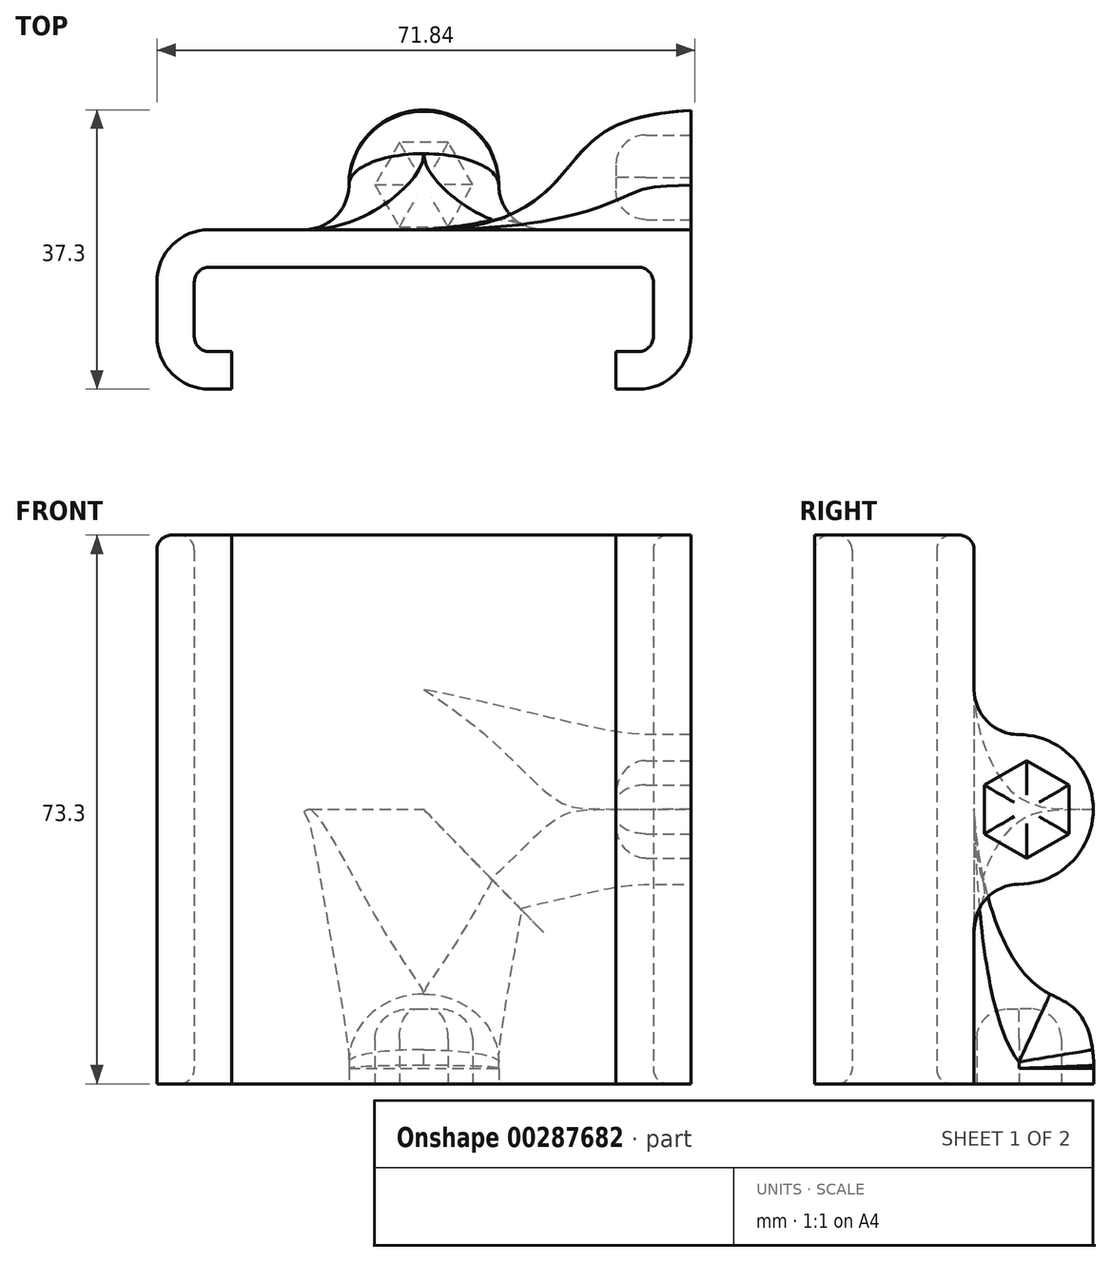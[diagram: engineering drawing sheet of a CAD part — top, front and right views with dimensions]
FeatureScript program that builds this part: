
annotation { "Feature Type Name" : "Feature", "Feature Type Description" : "" }
export const myFeature = defineFeature(function(context is Context, id is Id, definition is map)
    precondition{}
    {
        {
            var Q0;
            Q0=qCreatedBy(makeId("Top.planeOp"),FACE);
            var sketch = newSketch(context, id + "F0", { "sketchPlane" : qUnion([Q0])});
            skLineSegment(sketch, "E0.bottom", {"start": v(35.65, 10.65) * mm, "end": v(-35.65, 10.65) * mm});
            skLineSegment(sketch, "E0.top", {"start": v(35.65, -10.65) * mm, "end": v(25.65, -10.65) * mm});
            skLineSegment(sketch, "E0.left", {"start": v(35.65, 10.65) * mm, "end": v(35.65, -10.65) * mm});
            skLineSegment(sketch, "E0.right", {"start": v(-35.65, 10.65) * mm, "end": v(-35.65, -10.65) * mm});
            skPoint(sketch, "E0.middle", {"position": v(0, 0) * mm});
            skLineSegment(sketch, "E1.bottom", {"start": v(30.65, 5.65) * mm, "end": v(-30.65, 5.65) * mm});
            skLineSegment(sketch, "E1.top", {"start": v(30.65, -5.65) * mm, "end": v(25.65, -5.65) * mm});
            skLineSegment(sketch, "E1.left", {"start": v(30.65, 5.65) * mm, "end": v(30.65, -5.65) * mm});
            skLineSegment(sketch, "E1.right", {"start": v(-30.65, 5.65) * mm, "end": v(-30.65, -5.65) * mm});
            skLineSegment(sketch, "E2.left", {"start": v(-25.65, -10.65) * mm, "end": v(-25.65, -5.65) * mm});
            skLineSegment(sketch, "E2.right", {"start": v(25.65, -10.65) * mm, "end": v(25.65, -5.65) * mm});
            skLineSegment(sketch, "E3.trimOffspring", {"start": v(-25.65, -10.65) * mm, "end": v(-35.65, -10.65) * mm});
            skLineSegment(sketch, "E4.trimOffspring", {"start": v(-25.65, -5.65) * mm, "end": v(-30.65, -5.65) * mm});
            skSolve(sketch);
        }
        {
            var Q0;
            Q0=qSketchRegion(id+"F0",true);
            extrude(context, id + "F1", {"entities" : qUnion([Q0]), "endBound" : BoundingType.SYMMETRIC, "depth" : 73.3 * mm});
        }
        {
            var Q0;
            Q0=makeQuery(id+"F1.opExtrude","SWEPT_EDGE",EDGE,{"disambiguationData":[OSD([sQuery(id+"F0.wireOp",EDGE,"E1.bottom"),sQuery(id+"F0.wireOp",EDGE,"E1.right")])]});
            var Q1;
            Q1=makeQuery(id+"F1.opExtrude","SWEPT_EDGE",EDGE,{"disambiguationData":[OSD([sQuery(id+"F0.wireOp",EDGE,"E1.bottom"),sQuery(id+"F0.wireOp",EDGE,"E1.left")])]});
            var Q2;
            Q2=makeQuery(id+"F1.opExtrude","SWEPT_EDGE",EDGE,{"disambiguationData":[OSD([sQuery(id+"F0.wireOp",EDGE,"E1.top"),sQuery(id+"F0.wireOp",EDGE,"E1.left")])]});
            var Q3;
            Q3=makeQuery(id+"F1.opExtrude","SWEPT_EDGE",EDGE,{"disambiguationData":[OSD([sQuery(id+"F0.wireOp",EDGE,"E1.right"),sQuery(id+"F0.wireOp",EDGE,"E4.trimOffspring")])]});
            fillet(context, id + "F2", {"entities" : qUnion([Q0, Q1, Q2, Q3]), "radius" : 2 * mm, "tangentPropagation" : true, "allowEdgeOverflow" : false});
        }
        {
            var Q0;
            Q0=makeQuery(id+"F1.opExtrude","CAP_FACE",FACE,{"disambiguationData":[OSD([sQuery(id+"F0.wireOp",EDGE,"E0.bottom"),sQuery(id+"F0.wireOp",EDGE,"E0.top"),sQuery(id+"F0.wireOp",EDGE,"E0.left"),sQuery(id+"F0.wireOp",EDGE,"E0.right"),sQuery(id+"F0.wireOp",EDGE,"E1.bottom"),sQuery(id+"F0.wireOp",EDGE,"E1.top"),sQuery(id+"F0.wireOp",EDGE,"E1.left"),sQuery(id+"F0.wireOp",EDGE,"E1.right"),sQuery(id+"F0.wireOp",EDGE,"E2.left"),sQuery(id+"F0.wireOp",EDGE,"E2.right"),sQuery(id+"F0.wireOp",EDGE,"E3.trimOffspring"),sQuery(id+"F0.wireOp",EDGE,"E4.trimOffspring")])],"isStart":true});
            var sketch = newSketch(context, id + "F3", { "sketchPlane" : qUnion([Q0])});
            skArc(sketch, "E5", {"start": v(-10, -16.65) * mm, "mid": v(0, -26.65) * mm, "end": v(10, -16.65) * mm});
            skArc(sketch, "E6", {"start": v(16, -10.65) * mm, "mid": v(11.76, -12.4) * mm, "end": v(10, -16.65) * mm});
            skArc(sketch, "E7.MirrorC", {"start": v(-16, -10.65) * mm, "mid": v(-11.76, -12.4) * mm, "end": v(-10, -16.65) * mm});
            skLineSegment(sketch, "E8", {"start": v(16, -10.65) * mm, "end": v(-16, -10.65) * mm});
            skSolve(sketch);
        }
        {
            var Q0;
            Q0=makeQuery(id+"F1.opExtrude","SWEPT_FACE",FACE,{"disambiguationData":[OSD([sQuery(id+"F0.wireOp",EDGE,"E0.left")])]});
            var sketch = newSketch(context, id + "F4", { "sketchPlane" : qUnion([Q0])});
            skArc(sketch, "E9", {"start": v(16.65, -10) * mm, "mid": v(26.65, 0) * mm, "end": v(16.65, 10) * mm});
            skArc(sketch, "E10", {"start": v(10.65, 16) * mm, "mid": v(12.4, 11.76) * mm, "end": v(16.65, 10) * mm});
            skArc(sketch, "E11.MirrorC", {"start": v(10.65, -16) * mm, "mid": v(12.4, -11.76) * mm, "end": v(16.65, -10) * mm});
            skLineSegment(sketch, "E12", {"start": v(16.65, 16) * mm, "end": v(-29.2, 16) * mm, "construction": true});
            skLineSegment(sketch, "E13", {"start": v(-29.2, 16) * mm, "end": v(-29.2, -16) * mm, "construction": true});
            skLineSegment(sketch, "E14", {"start": v(-29.2, -16) * mm, "end": v(16.65, -16) * mm, "construction": true});
            skLineSegment(sketch, "E15", {"start": v(10.65, 16) * mm, "end": v(10.65, -16) * mm});
            skSolve(sketch);
        }
        {
            var Q0;
            Q0=qCreatedBy(makeId("Right.planeOp"),FACE);
            var sketch = newSketch(context, id + "F5", { "sketchPlane" : qUnion([Q0])});
            skFitSpline(sketch, "E16", {"points": [v(26.65, -36.65) * mm, v(19.37, -23.79) * mm, v(10.65, 0) * mm], "startDerivative": vector(2.18, 76.61) * mm, "endDerivative": vector(-4.53, 63.87) * mm});
            skLineSegment(sketch, "E17", {"start": v(26.65, -36.65) * mm, "end": v(42.74, -36.65) * mm});
            skLineSegment(sketch, "E18", {"start": v(42.74, -36.65) * mm, "end": v(42.74, 0) * mm});
            skLineSegment(sketch, "E19", {"start": v(10.65, 0) * mm, "end": v(10.65, 42.07) * mm});
            skLineSegment(sketch, "E20", {"start": v(10.65, 42.07) * mm, "end": v(42.74, 42.07) * mm});
            skLineSegment(sketch, "E21", {"start": v(42.74, 42.07) * mm, "end": v(42.74, 0) * mm});
            skSolve(sketch);
        }
        {
            var Q0;
            Q0=qCreatedBy(makeId("Top.planeOp"),FACE);
            var sketch = newSketch(context, id + "F6", { "sketchPlane" : qUnion([Q0])});
            skFitSpline(sketch, "E22", {"points": [v(0, 10.65) * mm, v(21.19, 21.2) * mm, v(41.65, 26.65) * mm], "startDerivative": vector(84.73, 0) * mm, "endDerivative": vector(76.42, -1.18) * mm});
            skLineSegment(sketch, "E23", {"start": v(0, 32.83) * mm, "end": v(41.65, 32.83) * mm});
            skLineSegment(sketch, "E24", {"start": v(41.65, 32.83) * mm, "end": v(41.65, 26.65) * mm});
            skLineSegment(sketch, "E25", {"start": v(0, 10.65) * mm, "end": v(-41.72, 10.65) * mm});
            skLineSegment(sketch, "E26", {"start": v(-41.72, 10.65) * mm, "end": v(-41.72, 32.83) * mm});
            skLineSegment(sketch, "E27", {"start": v(-41.72, 32.83) * mm, "end": v(0, 32.83) * mm});
            skSolve(sketch);
        }
        {
            var Q0;
            Q0=makeQuery(id+"F1.opExtrude","CAP_EDGE",EDGE,{"disambiguationData":[OSD([sQuery(id+"F0.wireOp",EDGE,"E0.left")])],"isStart":true});
            var Q1;
            Q1=makeQuery(id+"F1.opExtrude","CAP_VERTEX",VERTEX,{"disambiguationData":[OSD([sQuery(id+"F0.wireOp",EDGE,"E0.bottom"),sQuery(id+"F0.wireOp",EDGE,"E0.right")])],"isStart":false});
            cPlane(context, id + "F7", {"entities" : qUnion([Q0, Q1]), "cplaneType" : CPlaneType.LINE_ANGLE, "offset" : 25 * mm, "angle" : 0 * degree, "width" : 150 * mm, "height" : 150 * mm});
        }
        {
            var Q0;
            Q0=qSketchRegion(id+"F3",true);
            var Q1;
            Q1=qCreatedBy(id+"F7.planeOp",FACE);
            extrude(context, id + "F8", {"entities" : qUnion([Q0]), "operationType" : NewBodyOperationType.ADD, "endBound" : BoundingType.UP_TO_SURFACE, "oppositeDirection" : true, "endBoundEntityFace" : qUnion([Q1]), "depth" : 25 * mm});
        }
        {
            var Q0;
            Q0=qSketchRegion(id+"F4",true);
            var Q1;
            Q1=qCreatedBy(id+"F7.planeOp",FACE);
            extrude(context, id + "F9", {"entities" : qUnion([Q0]), "operationType" : NewBodyOperationType.ADD, "endBound" : BoundingType.UP_TO_SURFACE, "oppositeDirection" : true, "endBoundEntityFace" : qUnion([Q1]), "depth" : 25 * mm});
        }
        {
            var Q0;
            Q0=qSketchRegion(id+"F6",true);
            var Q1;
            Q1=qCreatedBy(id+"F7.planeOp",FACE);
            extrude(context, id + "F10", {"entities" : qUnion([Q0]), "operationType" : NewBodyOperationType.REMOVE, "endBound" : BoundingType.THROUGH_ALL, "depth" : 25 * mm, "hasSecondDirection" : true, "secondDirectionBound" : SecondDirectionBoundingType.UP_TO_SURFACE, "secondDirectionOppositeDirection" : true, "secondDirectionBoundEntityFace" : qUnion([Q1]), "secondDirectionDepth" : 25 * mm});
        }
        {
            var Q0;
            Q0=qSketchRegion(id+"F5",true);
            var Q1;
            Q1=qCreatedBy(id+"F7.planeOp",FACE);
            extrude(context, id + "F11", {"entities" : qUnion([Q0]), "operationType" : NewBodyOperationType.REMOVE, "endBound" : BoundingType.THROUGH_ALL, "oppositeDirection" : true, "depth" : 25 * mm, "hasSecondDirection" : true, "secondDirectionBound" : SecondDirectionBoundingType.UP_TO_SURFACE, "secondDirectionOppositeDirection" : false, "secondDirectionBoundEntityFace" : qUnion([Q1]), "secondDirectionDepth" : 25 * mm});
        }
        {
            var Q0;
            Q0=makeQuery(id+"F10.boolean.opBoolean","INTERSECT",EDGE,{"derivedFrom":[makeQuery(id+"F9.opExtrude","SWEPT_FACE",FACE,{"disambiguationData":[OSD([sQuery(id+"F4.wireOp",EDGE,"E9")])]}),makeQuery(id+"F10.opExtrude","SWEPT_FACE",FACE,{"disambiguationData":[OSD([sQuery(id+"F6.wireOp",EDGE,"E22")])]})]});
            fillet(context, id + "F12", {"entities" : qUnion([Q0]), "radius" : 10 * mm, "tangentPropagation" : true, "allowEdgeOverflow" : false});
        }
        {
            var Q0;
            Q0=makeQuery(id+"F11.boolean.opBoolean","INTERSECT",EDGE,{"derivedFrom":[makeQuery(id+"F8.opExtrude","SWEPT_FACE",FACE,{"disambiguationData":[OSD([sQuery(id+"F3.wireOp",EDGE,"E5")])]}),makeQuery(id+"F11.opExtrude","SWEPT_FACE",FACE,{"disambiguationData":[OSD([sQuery(id+"F5.wireOp",EDGE,"E16")])]})]});
            fillet(context, id + "F13", {"entities" : qUnion([Q0]), "radius" : 10 * mm, "tangentPropagation" : true, "allowEdgeOverflow" : false});
        }
        {
            var Q0;
            Q0=makeQuery(id+"F1.opExtrude","SWEPT_EDGE",EDGE,{"disambiguationData":[OSD([sQuery(id+"F0.wireOp",EDGE,"E0.bottom"),sQuery(id+"F0.wireOp",EDGE,"E0.right")])]});
            var Q1;
            Q1=makeQuery(id+"F1.opExtrude","SWEPT_EDGE",EDGE,{"disambiguationData":[OSD([sQuery(id+"F0.wireOp",EDGE,"E0.top"),sQuery(id+"F0.wireOp",EDGE,"E0.left")])]});
            var Q2;
            Q2=makeQuery(id+"F1.opExtrude","SWEPT_EDGE",EDGE,{"disambiguationData":[OSD([sQuery(id+"F0.wireOp",EDGE,"E0.right"),sQuery(id+"F0.wireOp",EDGE,"E3.trimOffspring")])]});
            fillet(context, id + "F14", {"entities" : qUnion([Q0, Q1, Q2]), "radius" : 7 * mm, "tangentPropagation" : true, "allowEdgeOverflow" : false});
        }
        {
            var Q0;
            Q0=makeQuery(id+"F3.imprint","IMPRINT",FACE,{"disambiguationData":[TD([[makeQuery(id+"F3.imprint","IMPRINT",EDGE,{"derivedFrom":sQuery(id+"F3.wireOp",EDGE,"E5")}),1.0]])]});
            var sketch = newSketch(context, id + "F15", { "sketchPlane" : qUnion([Q0])});
            skCircle(sketch, "E28.cCircle", {"center": v(0, -16.65) * mm, "radius": 5.65 * mm, "construction": true});
            skLineSegment(sketch, "E28.0", {"start": v(3.26, -11) * mm, "end": v(6.52, -16.65) * mm});
            skLineSegment(sketch, "E28.1", {"start": v(6.52, -16.65) * mm, "end": v(3.26, -22.3) * mm});
            skLineSegment(sketch, "E28.2", {"start": v(3.26, -22.3) * mm, "end": v(-3.26, -22.3) * mm});
            skLineSegment(sketch, "E28.3", {"start": v(-3.26, -22.3) * mm, "end": v(-6.52, -16.65) * mm});
            skLineSegment(sketch, "E28.4", {"start": v(-6.52, -16.65) * mm, "end": v(-3.26, -11) * mm});
            skLineSegment(sketch, "E28.5", {"start": v(-3.26, -11) * mm, "end": v(3.26, -11) * mm});
            skPoint(sketch, "E28.0.midPoint", {"position": v(4.9, -13.82) * mm});
            skSolve(sketch);
        }
        {
            var Q0;
            Q0=qSketchRegion(id+"F15",true);
            extrude(context, id + "F16", {"entities" : qUnion([Q0]), "operationType" : NewBodyOperationType.REMOVE, "oppositeDirection" : true, "depth" : 10 * mm});
        }
        {
            var Q0;
            Q0=makeQuery(id+"F16.boolean.opBoolean","COPY",FACE,{"derivedFrom":makeQuery(id+"F16.opExtrude","CAP_FACE",FACE,{"disambiguationData":[OSD([sQuery(id+"F15.wireOp",EDGE,"E28.0"),sQuery(id+"F15.wireOp",EDGE,"E28.1"),sQuery(id+"F15.wireOp",EDGE,"E28.2"),sQuery(id+"F15.wireOp",EDGE,"E28.3"),sQuery(id+"F15.wireOp",EDGE,"E28.4"),sQuery(id+"F15.wireOp",EDGE,"E28.5")])],"isStart":false})});
            fillet(context, id + "F17", {"entities" : qUnion([Q0]), "radius" : 4 * mm, "tangentPropagation" : true, "allowEdgeOverflow" : false});
        }
        {
            var Q0;
            Q0=makeQuery(id+"F9.boolean.opBoolean","MERGE",FACE,{"derivedFrom":[makeQuery(id+"F1.opExtrude","SWEPT_FACE",FACE,{"disambiguationData":[OSD([sQuery(id+"F0.wireOp",EDGE,"E0.left")])]}),makeQuery(id+"F9.opExtrude","CAP_FACE",FACE,{"disambiguationData":[OSD([sQuery(id+"F4.wireOp",EDGE,"E9"),sQuery(id+"F4.wireOp",EDGE,"E10"),sQuery(id+"F4.wireOp",EDGE,"E11.MirrorC"),sQuery(id+"F4.wireOp",EDGE,"E15")])],"isStart":true})]});
            var sketch = newSketch(context, id + "F18", { "sketchPlane" : qUnion([Q0])});
            skCircle(sketch, "E29.cCircle", {"center": v(17.65, 0) * mm, "radius": 5.65 * mm, "construction": true});
            skLineSegment(sketch, "E29.0", {"start": v(17.65, -6.52) * mm, "end": v(12, -3.26) * mm});
            skLineSegment(sketch, "E29.1", {"start": v(12, -3.26) * mm, "end": v(12, 3.26) * mm});
            skLineSegment(sketch, "E29.2", {"start": v(12, 3.26) * mm, "end": v(17.65, 6.52) * mm});
            skLineSegment(sketch, "E29.3", {"start": v(17.65, 6.52) * mm, "end": v(23.3, 3.26) * mm});
            skLineSegment(sketch, "E29.4", {"start": v(23.3, 3.26) * mm, "end": v(23.3, -3.26) * mm});
            skLineSegment(sketch, "E29.5", {"start": v(23.3, -3.26) * mm, "end": v(17.65, -6.52) * mm});
            skPoint(sketch, "E29.0.midPoint", {"position": v(14.82, -4.9) * mm});
            skSolve(sketch);
        }
        {
            var Q0;
            Q0=qSketchRegion(id+"F18",true);
            extrude(context, id + "F19", {"entities" : qUnion([Q0]), "operationType" : NewBodyOperationType.REMOVE, "oppositeDirection" : true, "depth" : 10 * mm});
        }
        {
            var Q0;
            Q0=makeQuery(id+"F19.boolean.opBoolean","COPY",FACE,{"derivedFrom":makeQuery(id+"F19.opExtrude","CAP_FACE",FACE,{"disambiguationData":[OSD([sQuery(id+"F18.wireOp",EDGE,"E29.0"),sQuery(id+"F18.wireOp",EDGE,"E29.1"),sQuery(id+"F18.wireOp",EDGE,"E29.2"),sQuery(id+"F18.wireOp",EDGE,"E29.3"),sQuery(id+"F18.wireOp",EDGE,"E29.4"),sQuery(id+"F18.wireOp",EDGE,"E29.5")])],"isStart":false})});
            fillet(context, id + "F20", {"entities" : qUnion([Q0]), "radius" : 4 * mm, "tangentPropagation" : true, "allowEdgeOverflow" : false});
        }
        {
            var Q0;
            Q0=makeQuery(id+"F1.opExtrude","CAP_EDGE",EDGE,{"disambiguationData":[OSD([sQuery(id+"F0.wireOp",EDGE,"E0.bottom")])],"isStart":false});
            var Q1;
            Q1=makeQuery(id+"F1.opExtrude","CAP_EDGE",EDGE,{"disambiguationData":[OSD([sQuery(id+"F0.wireOp",EDGE,"E1.bottom")])],"isStart":false});
            var Q2;
            Q2=makeQuery(id+"F1.opExtrude","CAP_EDGE",EDGE,{"disambiguationData":[OSD([sQuery(id+"F0.wireOp",EDGE,"E1.bottom")])],"isStart":true});
            fillet(context, id + "F21", {"entities" : qUnion([Q0, Q1, Q2]), "radius" : 2 * mm, "tangentPropagation" : true, "allowEdgeOverflow" : false});
        }
    });
